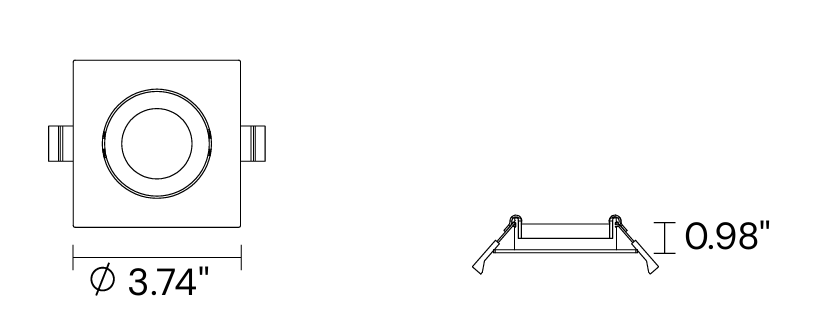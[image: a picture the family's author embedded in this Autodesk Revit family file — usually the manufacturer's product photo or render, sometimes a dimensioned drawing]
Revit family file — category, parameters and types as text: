
# Revit family: Alcon-14119-S-ADJ-Revit-Family
name_source: partatom
category: Lighting Fixtures
units: mm (PartAtom-declared; Revit-internal decimal feet)

## family parameters
Always vertical = Yes
Cut with Voids When Loaded = No
Host = Ceiling
Light Source = Yes
OmniClass Number = 23.80.70.11
OmniClass Title = Luminaries for Internal Lighting
Part Type = Normal
Room Calculation Point = No
Round Connector Dimension = Use Diameter
Shared = No

## types (1)
- Type 1
    Color Filter = 16777215
    Default Elevation = 0' - 0"
    Dimming Lamp Color Temperature Shift = <None>
    Engine = Default
    Housing = Default
    Lens = <By Category>
    Light Source = Light Source
    Light Source Symbol Length = 10' - 0"
    Link To Product Page = https://www.alconlighting.com
    Manufacturer = Alcon Light
    Metal = <By Category>
    Product Identity = Alcon Lighting 14119-S-ADJ
    Spot Beam Angle = 30.00°
    Spot Field Angle = 90.00°
    Tilt Angle = 60.00°

## geometry (parser evidence)
native form markers: Sweep x2
no freeform markers — native parametric forms only
